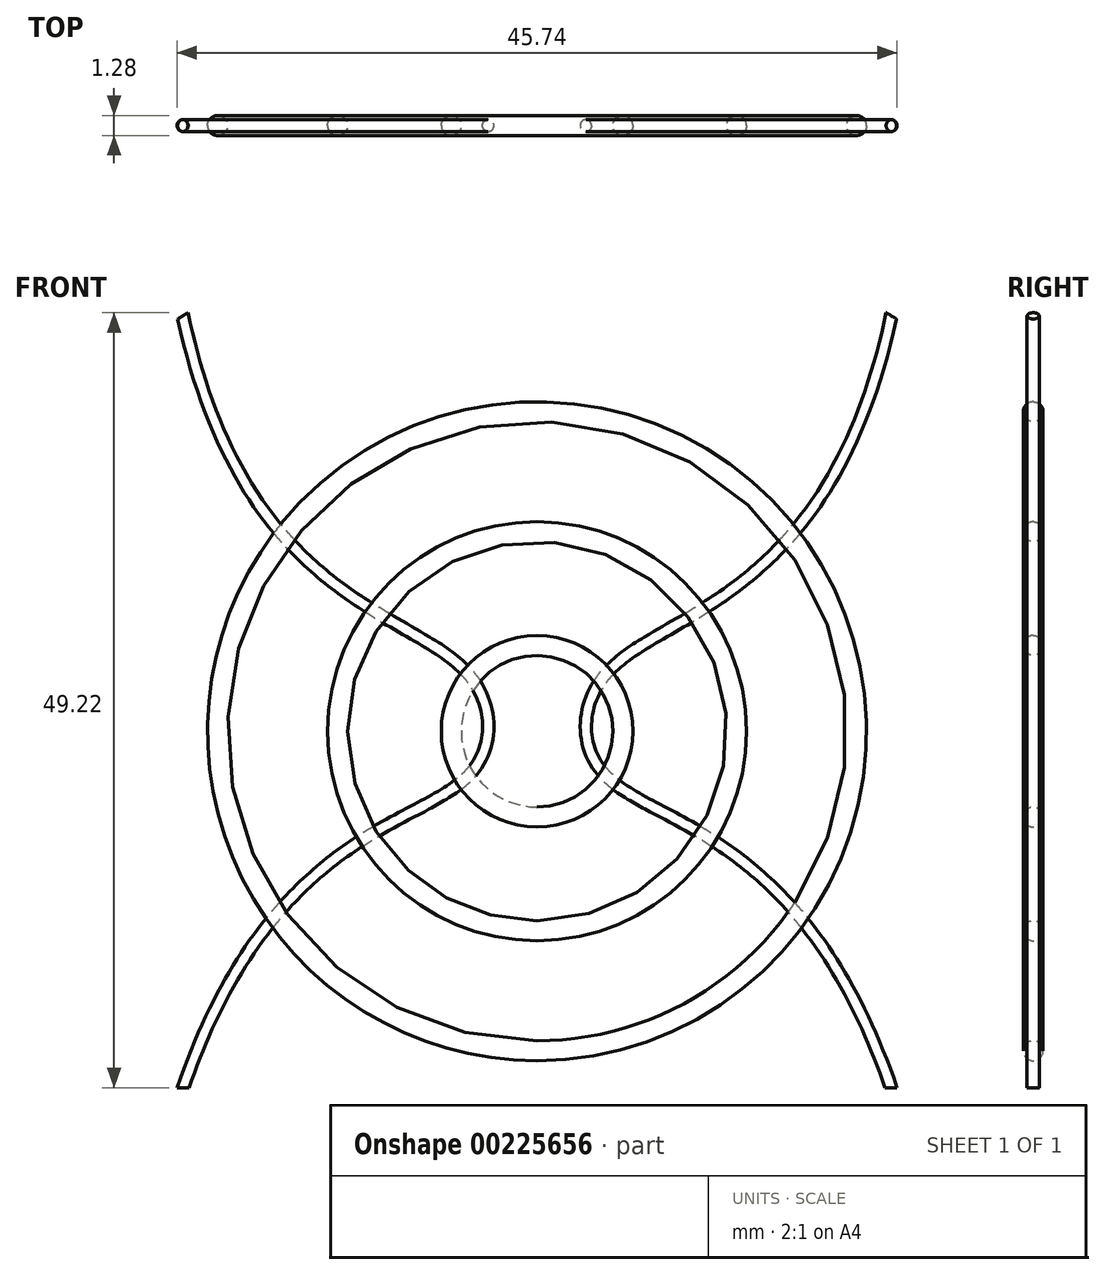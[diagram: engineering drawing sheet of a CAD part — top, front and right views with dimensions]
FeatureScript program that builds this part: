
annotation { "Feature Type Name" : "Feature", "Feature Type Description" : "" }
export const myFeature = defineFeature(function(context is Context, id is Id, definition is map)
    precondition{}
    {
        {
            var Q0;
            Q0=qCreatedBy(makeId("Front.planeOp"),FACE);
            var sketch = newSketch(context, id + "F0", { "sketchPlane" : qUnion([Q0])});
            skFitSpline(sketch, "E0", {"points": [v(-22.56, 26.35) * mm, v(-4.47, 3.64) * mm, v(-4.14, -2.46) * mm, v(-22.56, -22.64) * mm], "startDerivative": vector(28.54, -132.5) * mm, "endDerivative": vector(-43.85, -126.24) * mm});
            skLineSegment(sketch, "E1", {"start": v(-22.56, 26.35) * mm, "end": v(-22.56, -22.64) * mm, "construction": true});
            skLineSegment(sketch, "E2", {"start": v(-22.56, -31.77) * mm, "end": v(-22.56, -73.83) * mm, "construction": true});
            skLineSegment(sketch, "E3", {"start": v(0, 40.1) * mm, "end": v(-65.8, 0) * mm, "construction": true});
            skLineSegment(sketch, "E4", {"start": v(0, 0) * mm, "end": v(0, 15) * mm});
            skLineSegment(sketch, "E5", {"start": v(0, 15) * mm, "end": v(0, -20.5) * mm, "construction": true});
            skSolve(sketch);
        }
        {
            var Q0;
            Q0=sQuery(id+"F0.wireOp",EDGE,"E3");
            var Q1;
            Q1=qCreatedBy(makeId("Top.planeOp"),FACE);
            cPlane(context, id + "F1", {"entities" : qUnion([Q0, Q1]), "cplaneType" : CPlaneType.LINE_ANGLE, "offset" : 25.4 * mm, "angle" : 0 * degree, "flipAlignment" : true, "width" : 152.4 * mm, "height" : 152.4 * mm});
        }
        {
            var Q0;
            Q0=qCreatedBy(id+"F1.planeOp",FACE);
            var sketch = newSketch(context, id + "F2", { "sketchPlane" : qUnion([Q0])});
            skCircle(sketch, "E6", {"center": v(-5.49, 0) * mm, "radius": 0.38 * mm});
            skSolve(sketch);
        }
        {
            var Q0;
            Q0=makeQuery(id+"F2.imprint","IMPRINT",FACE,{"disambiguationData":[TD([[makeQuery(id+"F2.imprint","IMPRINT",EDGE,{"derivedFrom":sQuery(id+"F2.wireOp",EDGE,"E6")}),1.0]])]});
            var Q1;
            Q1=sQuery(id+"F0.wireOp",EDGE,"E0");
            sweep(context, id + "F3", {"profiles" : qUnion([Q0]), "path" : qUnion([Q1])});
        }
        {
            var Q0;
            Q0=qCreatedBy(makeId("Front.planeOp"),FACE);
            var sketch = newSketch(context, id + "F4", { "sketchPlane" : qUnion([Q0])});
            skCircle(sketch, "E7", {"center": v(0, 0) * mm, "radius": 20.32 * mm});
            skCircle(sketch, "E8", {"center": v(0, 0) * mm, "radius": 12.7 * mm});
            skCircle(sketch, "E9", {"center": v(0, 0) * mm, "radius": 5.45 * mm});
            skSolve(sketch);
        }
        {
            var Q0;
            Q0=qCreatedBy(makeId("Right.planeOp"),FACE);
            var sketch = newSketch(context, id + "F5", { "sketchPlane" : qUnion([Q0])});
            skCircle(sketch, "E10", {"center": v(0, 20.3) * mm, "radius": 0.64 * mm});
            skCircle(sketch, "E11.0.1.0", {"center": v(0, 12.67) * mm, "radius": 0.64 * mm});
            skLineSegment(sketch, "E11.direction1", {"start": v(0, 20.3) * mm, "end": v(0.63, 20.3) * mm, "construction": true});
            skLineSegment(sketch, "E11.direction2", {"start": v(0, 20.3) * mm, "end": v(0, 12.67) * mm, "construction": true});
            skCircle(sketch, "E12.0.1.0", {"center": v(0, 5.45) * mm, "radius": 0.64 * mm});
            skLineSegment(sketch, "E12.direction1", {"start": v(0, 12.67) * mm, "end": v(15.62, 12.67) * mm, "construction": true});
            skLineSegment(sketch, "E12.direction2", {"start": v(0, 12.67) * mm, "end": v(-0.03, 5.18) * mm, "construction": true});
            skSolve(sketch);
        }
        {
            var Q0;
            Q0=makeQuery(id+"F5.imprint","IMPRINT",FACE,{"disambiguationData":[TD([[makeQuery(id+"F5.imprint","IMPRINT",EDGE,{"derivedFrom":sQuery(id+"F5.wireOp",EDGE,"E10")}),1.0]])]});
            var Q1;
            Q1=makeQuery(id+"F5.imprint","IMPRINT",FACE,{"disambiguationData":[TD([[makeQuery(id+"F5.imprint","IMPRINT",EDGE,{"derivedFrom":sQuery(id+"F5.wireOp",EDGE,"E11.0.1.0")}),1.0]])]});
            var Q2;
            Q2=makeQuery(id+"F5.imprint","IMPRINT",FACE,{"disambiguationData":[TD([[makeQuery(id+"F5.imprint","IMPRINT",EDGE,{"derivedFrom":sQuery(id+"F5.wireOp",EDGE,"E12.0.1.0")}),1.0]])]});
            var Q3;
            Q3=sQuery(id+"F4.wireOp",EDGE,"E7");
            sweep(context, id + "F6", {"profiles" : qUnion([Q0, Q1, Q2]), "path" : qUnion([Q3])});
        }
        {
            var Q0;
            Q0=makeQuery(id+"F3.opSweep","SWEPT_BODY",BODY,{"disambiguationData":[OSD([sQuery(id+"F0.wireOp",EDGE,"E0"),sQuery(id+"F2.wireOp",EDGE,"E6")])]});
            var Q1;
            Q1=qCreatedBy(makeId("Right.planeOp"),FACE);
            mirror(context, id + "F7", {"entities" : qUnion([Q0]), "mirrorPlane" : qUnion([Q1])});
        }
    });
